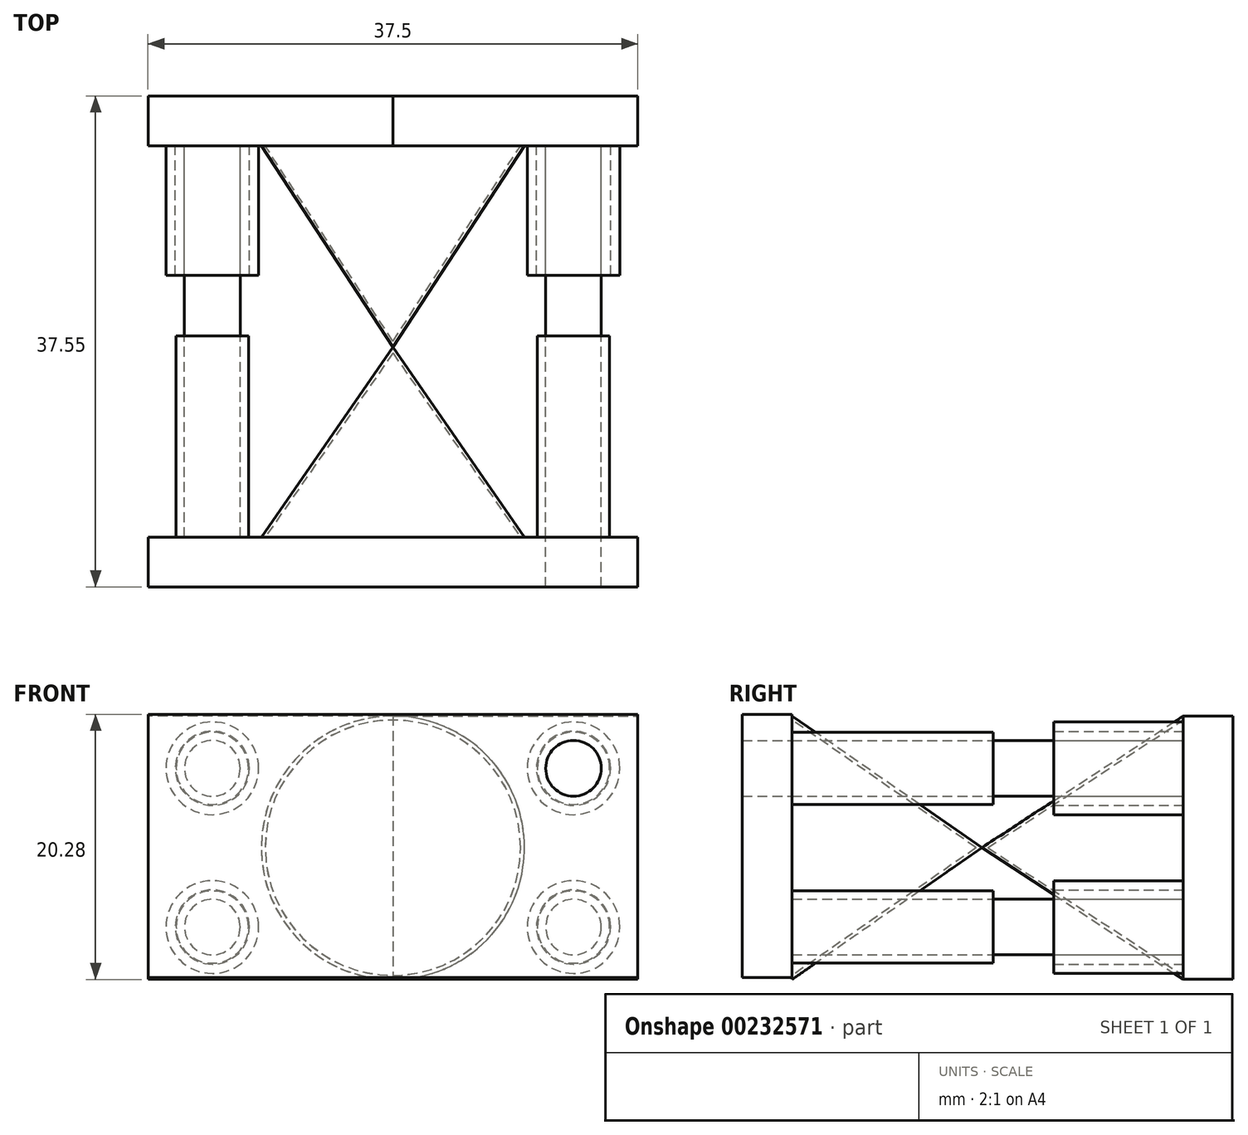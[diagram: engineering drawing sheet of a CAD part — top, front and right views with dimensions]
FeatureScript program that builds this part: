
annotation { "Feature Type Name" : "Feature", "Feature Type Description" : "" }
export const myFeature = defineFeature(function(context is Context, id is Id, definition is map)
    precondition{}
    {
        {
            var Q0;
            Q0=qCreatedBy(makeId("Top.planeOp"),FACE);
            var sketch = newSketch(context, id + "F0", { "sketchPlane" : qUnion([Q0])});
            skLineSegment(sketch, "E0.bottom", {"start": v(0, 25.78) * mm, "end": v(-10.08, 25.78) * mm});
            skLineSegment(sketch, "E1", {"start": v(0, 25.78) * mm, "end": v(0, 40.3) * mm});
            skLineSegment(sketch, "E2", {"start": v(-10.08, 25.78) * mm, "end": v(0, 40.3) * mm});
            skLineSegment(sketch, "E3", {"start": v(0, 40.3) * mm, "end": v(-10.08, 55.71) * mm});
            skLineSegment(sketch, "E4", {"start": v(-10.08, 55.71) * mm, "end": v(0, 55.71) * mm});
            skLineSegment(sketch, "E5", {"start": v(0, 40.3) * mm, "end": v(0, 55.71) * mm});
            skSolve(sketch);
        }
        {
            var Q0;
            Q0 = qSketchRegion(id + "F0", true);
            var Q1;
            Q1=sQuery(id+"F0.wireOp",EDGE,"E5");
            revolve(context, id + "F1", {"entities" : qUnion([Q0]), "axis" : qUnion([Q1]), "revolveType" : RevolveType.FULL});
        }
        {
            var Q0;
            Q0=makeQuery(id+"F1.opRevolve","SWEPT_FACE",FACE,{"disambiguationData":[OSD([sQuery(id+"F0.wireOp",EDGE,"E4")])]});
            shell(context, id + "F2", {"entities" : qUnion([Q0]), "thickness" : 0.25 * mm});
        }
        {
            var Q0;
            Q0=makeQuery(id+"F1.opRevolve","SWEPT_FACE",FACE,{"disambiguationData":[OSD([sQuery(id+"F0.wireOp",EDGE,"E4")])]});
            var sketch = newSketch(context, id + "F3", { "sketchPlane" : qUnion([Q0])});
            skLineSegment(sketch, "E6.bottom", {"start": v(0, 10.08) * mm, "end": v(-18.75, 10.08) * mm});
            skLineSegment(sketch, "E6.top", {"start": v(0, -10.08) * mm, "end": v(-18.75, -10.08) * mm});
            skLineSegment(sketch, "E6.left", {"start": v(0, 10.08) * mm, "end": v(0, -10.08) * mm});
            skLineSegment(sketch, "E6.right", {"start": v(-18.75, 10.08) * mm, "end": v(-18.75, -10.08) * mm});
            skSolve(sketch);
        }
        {
            var Q0;
            Q0 = qSketchRegion(id + "F3", true);
            extrude(context, id + "F4", {"entities" : qUnion([Q0]), "depth" : 3.8 * mm});
        }
        {
            var Q0;
            Q0=makeQuery(id+"F4.opExtrude","CAP_FACE",FACE,{"disambiguationData":[OSD([sQuery(id+"F3.wireOp",EDGE,"E6.bottom"),sQuery(id+"F3.wireOp",EDGE,"E6.top"),sQuery(id+"F3.wireOp",EDGE,"E6.left"),sQuery(id+"F3.wireOp",EDGE,"E6.right")])],"isStart":true});
            var sketch = newSketch(context, id + "F5", { "sketchPlane" : qUnion([Q0])});
            skCircle(sketch, "E7", {"center": v(13.82, 6.07) * mm, "radius": 2.13 * mm});
            skLineSegment(sketch, "E8", {"start": v(10, 0) * mm, "end": v(18.75, 0) * mm});
            skCircle(sketch, "E9.MirrorC", {"center": v(13.82, -6.07) * mm, "radius": 2.13 * mm});
            skCircle(sketch, "E10", {"center": v(13.82, 6.07) * mm, "radius": 2.84 * mm});
            skCircle(sketch, "E11", {"center": v(13.82, 6.07) * mm, "radius": 3.55 * mm});
            skSolve(sketch);
        }
        {
            var Q0;
            Q0=makeQuery(id+"F5.imprint","IMPRINT",FACE,{"disambiguationData":[TD([[makeQuery(id+"F5.imprint","IMPRINT",EDGE,{"derivedFrom":sQuery(id+"F5.wireOp",EDGE,"E7")}),1.0]])]});
            var Q1;
            Q1=makeQuery(id+"F1.opRevolve","SWEPT_FACE",FACE,{"disambiguationData":[OSD([sQuery(id+"F0.wireOp",EDGE,"E0.bottom")])]});
            extrude(context, id + "F6", {"entities" : qUnion([Q0]), "endBound" : BoundingType.UP_TO_SURFACE, "endBoundEntityFace" : qUnion([Q1]), "depth" : 25.4 * mm});
        }
        {
            var Q0;
            Q0=sQuery(id+"F5.wireOp",EDGE,"E10");
            extrude(context, id + "F7", {"bodyType" : ToolBodyType.SURFACE, "surfaceEntities" : qUnion([Q0]), "depth" : 10.26 * mm});
        }
        {
            var Q0;
            Q0=makeQuery(id+"F5.imprint","IMPRINT",FACE,{"disambiguationData":[TD([[makeQuery(id+"F5.imprint","IMPRINT",EDGE,{"derivedFrom":sQuery(id+"F5.wireOp",EDGE,"E10")}),-1.0]])]});
            extrude(context, id + "F8", {"entities" : qUnion([Q0]), "operationType" : NewBodyOperationType.ADD, "depth" : 9.9 * mm});
        }
        {
            var Q0;
            Q0=makeQuery(id+"F6.opExtrude","CAP_FACE",FACE,{"disambiguationData":[OSD([sQuery(id+"F5.wireOp",EDGE,"E7")])],"isStart":false});
            var sketch = newSketch(context, id + "F9", { "sketchPlane" : qUnion([Q0])});
            skCircle(sketch, "E12", {"center": v(13.82, 6.07) * mm, "radius": 2.76 * mm});
            skSolve(sketch);
        }
        {
            var Q0;
            Q0 = qSketchRegion(id + "F9", true);
            extrude(context, id + "F10", {"entities" : qUnion([Q0]), "oppositeDirection" : true, "depth" : 15.4 * mm});
        }
        {
            var Q0;
            Q0=makeQuery(id+"F4.opExtrude","SWEPT_BODY",BODY,{"disambiguationData":[OSD([sQuery(id+"F3.wireOp",EDGE,"E6.bottom"),sQuery(id+"F3.wireOp",EDGE,"E6.top"),sQuery(id+"F3.wireOp",EDGE,"E6.left"),sQuery(id+"F3.wireOp",EDGE,"E6.right")])]});
            var Q1;
            Q1=makeQuery(id+"F6.opExtrude","SWEPT_BODY",BODY,{"disambiguationData":[OSD([sQuery(id+"F5.wireOp",EDGE,"E7")])]});
            var Q2;
            Q2=makeQuery(id+"F6.opExtrude","SWEPT_BODY",BODY,{"disambiguationData":[OSD([sQuery(id+"F5.wireOp",EDGE,"E9.MirrorC")])]});
            var Q3;
            Q3=makeQuery(id+"F10.opExtrude","SWEPT_BODY",BODY,{"disambiguationData":[OSD([sQuery(id+"F9.wireOp",EDGE,"E12")])]});
            var Q4;
            Q4=makeQuery(id+"F4.opExtrude","SWEPT_FACE",FACE,{"disambiguationData":[OSD([sQuery(id+"F3.wireOp",EDGE,"E6.left")])]});
            mirror(context, id + "F11", {"entities" : qUnion([Q0, Q1, Q2, Q3]), "mirrorPlane" : qUnion([Q4])});
        }
        {
            var Q0;
            Q0=makeQuery(id+"F6.opExtrude","SWEPT_BODY",BODY,{"disambiguationData":[OSD([sQuery(id+"F5.wireOp",EDGE,"E7")])]});
            var Q1;
            Q1=makeQuery(id+"F10.opExtrude","SWEPT_BODY",BODY,{"disambiguationData":[OSD([sQuery(id+"F9.wireOp",EDGE,"E12")])]});
            var Q2;
            Q2=makeQuery(id+"F4.opExtrude","SWEPT_BODY",BODY,{"disambiguationData":[OSD([sQuery(id+"F3.wireOp",EDGE,"E6.bottom"),sQuery(id+"F3.wireOp",EDGE,"E6.top"),sQuery(id+"F3.wireOp",EDGE,"E6.left"),sQuery(id+"F3.wireOp",EDGE,"E6.right")])]});
            var Q3;
            Q3=qCreatedBy(makeId("Top.planeOp"),FACE);
            mirror(context, id + "F12", {"entities" : qUnion([Q0, Q1, Q2]), "mirrorPlane" : qUnion([Q3])});
        }
        {
            var Q0;
            Q0=makeQuery(id+"F11.opPattern","COPY",BODY,{"derivedFrom":makeQuery(id+"F4.opExtrude","SWEPT_BODY",BODY,{"disambiguationData":[OSD([sQuery(id+"F3.wireOp",EDGE,"E6.bottom"),sQuery(id+"F3.wireOp",EDGE,"E6.top"),sQuery(id+"F3.wireOp",EDGE,"E6.left"),sQuery(id+"F3.wireOp",EDGE,"E6.right")])]}),"instanceName":"1"});
            var Q1;
            Q1=makeQuery(id+"F11.opPattern","COPY",BODY,{"derivedFrom":makeQuery(id+"F6.opExtrude","SWEPT_BODY",BODY,{"disambiguationData":[OSD([sQuery(id+"F5.wireOp",EDGE,"E7")])]}),"instanceName":"1"});
            var Q2;
            Q2=makeQuery(id+"F11.opPattern","COPY",BODY,{"derivedFrom":makeQuery(id+"F10.opExtrude","SWEPT_BODY",BODY,{"disambiguationData":[OSD([sQuery(id+"F9.wireOp",EDGE,"E12")])]}),"instanceName":"1"});
            var Q3;
            Q3=qCreatedBy(makeId("Top.planeOp"),FACE);
            mirror(context, id + "F13", {"entities" : qUnion([Q0, Q1, Q2]), "mirrorPlane" : qUnion([Q3])});
        }
        {
            var Q0;
            Q0=makeQuery(id+"F1.opRevolve","SWEPT_FACE",FACE,{"disambiguationData":[OSD([sQuery(id+"F0.wireOp",EDGE,"E0.bottom")])]});
            shell(context, id + "F14", {"entities" : qUnion([Q0]), "thickness" : 0.25 * mm});
        }
        {
            var Q0;
            Q0=makeQuery(id+"F6.opExtrude","CAP_FACE",FACE,{"disambiguationData":[OSD([sQuery(id+"F5.wireOp",EDGE,"E7")])],"isStart":false});
            var sketch = newSketch(context, id + "F15", { "sketchPlane" : qUnion([Q0])});
            skLineSegment(sketch, "E13.bottom", {"start": v(0, -9.94) * mm, "end": v(18.75, -9.94) * mm});
            skLineSegment(sketch, "E13.top", {"start": v(0, 10.2) * mm, "end": v(18.75, 10.2) * mm});
            skLineSegment(sketch, "E13.left", {"start": v(0, -9.94) * mm, "end": v(0, 10.2) * mm});
            skLineSegment(sketch, "E13.right", {"start": v(18.75, -9.94) * mm, "end": v(18.75, 10.2) * mm});
            skLineSegment(sketch, "E14.MirrorCS", {"start": v(0, 10.2) * mm, "end": v(-18.75, 10.2) * mm});
            skLineSegment(sketch, "E15.MirrorCS", {"start": v(-18.75, -9.94) * mm, "end": v(-18.75, 10.2) * mm});
            skLineSegment(sketch, "E16.MirrorCS", {"start": v(0, -9.94) * mm, "end": v(-18.75, -9.94) * mm});
            skSolve(sketch);
        }
        {
            var Q0;
            Q0=makeQuery(id+"F15.imprint","IMPRINT",FACE,{"disambiguationData":[TD([[makeQuery(id+"F15.imprint","IMPRINT",EDGE,{"derivedFrom":sQuery(id+"F15.wireOp",EDGE,"E13.bottom")}),1.0]])]});
            var Q1;
            Q1=makeQuery(id+"F15.imprint","IMPRINT",FACE,{"disambiguationData":[TD([[makeQuery(id+"F15.imprint","IMPRINT",EDGE,{"derivedFrom":sQuery(id+"F15.wireOp",EDGE,"E13.left")}),1.0]])]});
            extrude(context, id + "F16", {"entities" : qUnion([Q0, Q1]), "depth" : 3.8 * mm});
        }
    });
